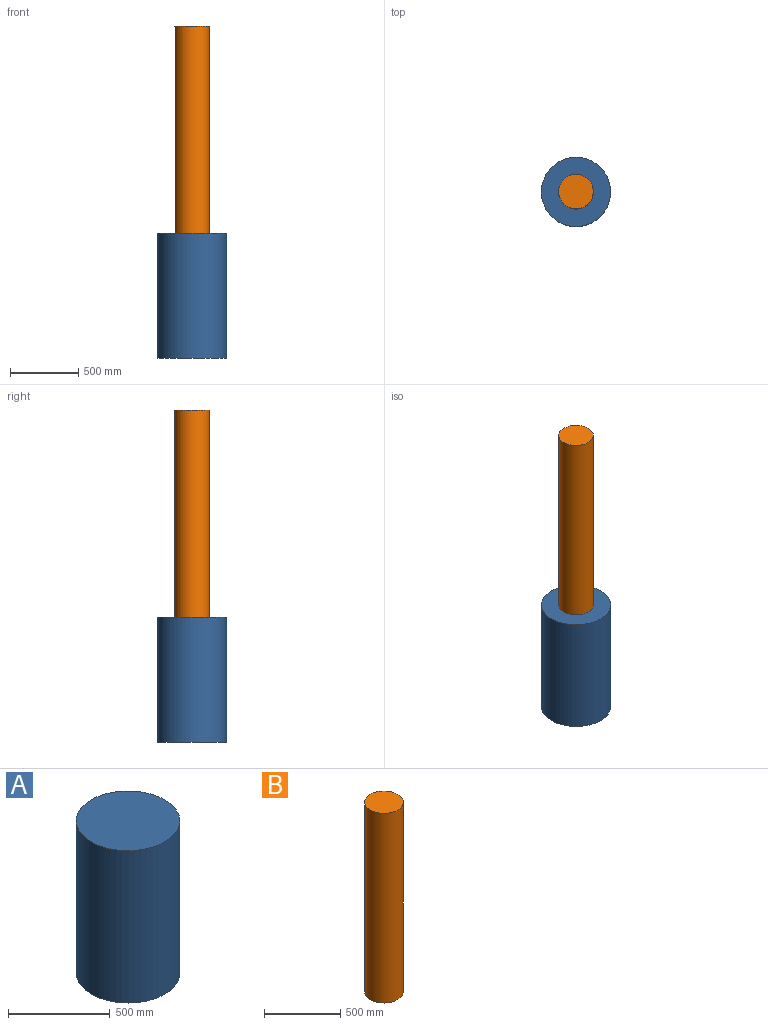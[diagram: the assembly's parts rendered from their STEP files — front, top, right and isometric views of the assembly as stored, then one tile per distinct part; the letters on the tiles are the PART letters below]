
ASSEMBLY  parts=2 mates=1
PART A: 3 faces, bbox 508x508x914.4 mm
  f0: cylinder r=254mm len=914.4mm, axis (0,0,-1), area 1459317.5mm2, adj f1,f2
  f1: plane 508x508mm, normal (0,0,1), area 202683mm2, adj f0
  f2: plane 508x508mm, normal (0,0,-1), area 202683mm2, adj f0
PART B: 3 faces, bbox 254x254x1524 mm
  f0: cylinder r=127mm len=1524mm, axis (0,0,-1), area 1216097.9mm2, adj f1,f2
  f1: plane 254x254mm, normal (0,0,1), area 50670.7mm2, adj f0
  f2: plane 254x254mm, normal (0,0,-1), area 50670.7mm2, adj f0
PLACE A t=(-294.16,204.83,-200.01)mm
PLACE B t=(-299.04,222.15,714.39)mm
MATE fastened B.f0 <-> A.f0  axis (0,0,-1) through (-299.04,222.15,714.39)mm
